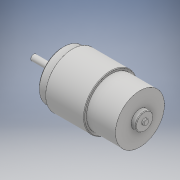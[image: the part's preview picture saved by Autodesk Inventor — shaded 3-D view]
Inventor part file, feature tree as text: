
AUTODESK INVENTOR PART (.ipt)
format: ipt  version: 2017 (Build 210142000, 142)  size: 163,840 bytes
history: native  units: mm
features: other x1, revolve x1, chamfer x1, fillet x1, sketch x1
ambient origin geometry x8: Origin, YZ Plane, XZ Plane, XY Plane, X Axis, Y Axis, Z Axis, Center Point
bodies: Body1 (feature_tree)
feature tree (5):
  other  "ソリッド1"
  revolve  "回転1"
  chamfer  "面取り1"  Distance=4.2mm
  fillet  "フィレット1"  Radius=21.05mm
  sketch  "スケッチ1"
